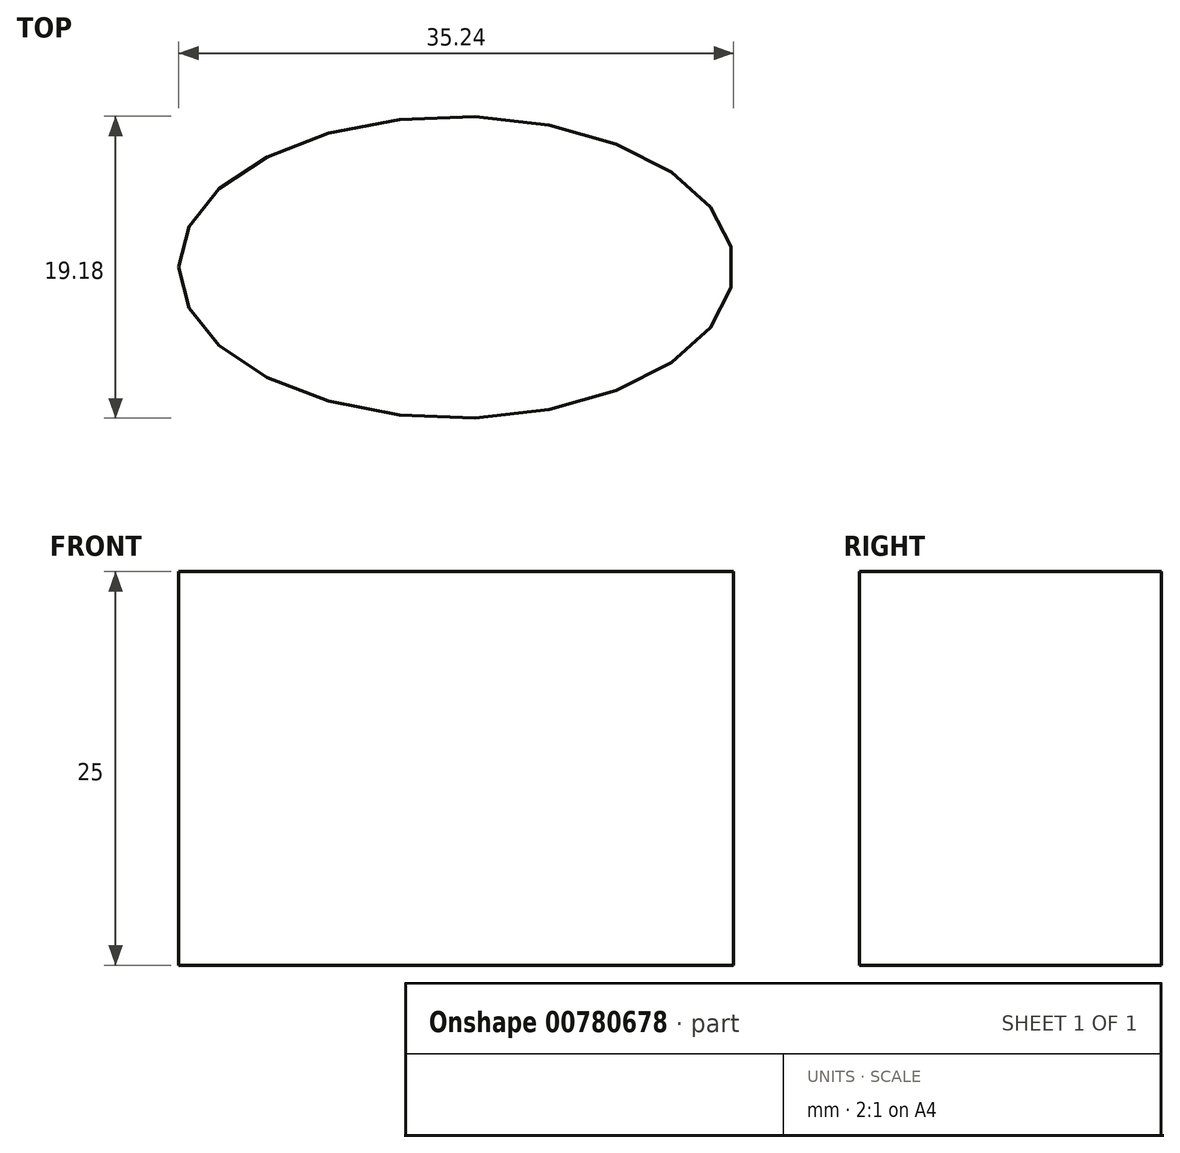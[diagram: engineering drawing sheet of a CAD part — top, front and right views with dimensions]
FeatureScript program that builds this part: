
annotation { "Feature Type Name" : "Feature", "Feature Type Description" : "" }
export const myFeature = defineFeature(function(context is Context, id is Id, definition is map)
    precondition{}
    {
        {
            var Q0;
            Q0=qCreatedBy(makeId("Top.planeOp"),FACE);
            var sketch = newSketch(context, id + "F0", { "sketchPlane" : qUnion([Q0])});
            skCircle(sketch, "E0", {"center": v(0, 0) * mm, "radius": 63.04 * mm, "construction": true});
            skEllipse(sketch, "E1", {"center": v(63.04, 0) * mm, "majorRadius": 17.62 * mm, "minorRadius": 9.59 * mm, "majorAxis": v(-1, 0), "construction": true});
            skLineSegment(sketch, "E2", {"start": v(0, 0) * mm, "end": v(58.12, 9.2) * mm, "construction": true});
            skSolve(sketch);
        }
        {
            var Q0;
            Q0=qCreatedBy(makeId("Top.planeOp"),FACE);
            var sketch = newSketch(context, id + "F1", { "sketchPlane" : qUnion([Q0])});
            skEllipse(sketch, "E3.0", {"center": v(63.04, 0) * mm, "majorRadius": 17.62 * mm, "minorRadius": 9.59 * mm, "majorAxis": v(-1, 0)});
            skSolve(sketch);
        }
        {
            var Q0;
            Q0=makeQuery(id+"F1.imprint","IMPRINT",FACE,{"disambiguationData":[TD([[makeQuery(id+"F1.imprint","IMPRINT",EDGE,{"derivedFrom":sQuery(id+"F1.wireOp",EDGE,"E3.0")}),1.0]])]});
            extrude(context, id + "F2", {"entities" : qUnion([Q0]), "depth" : 25 * mm, "offsetDistance" : 25 * mm});
        }
    });
